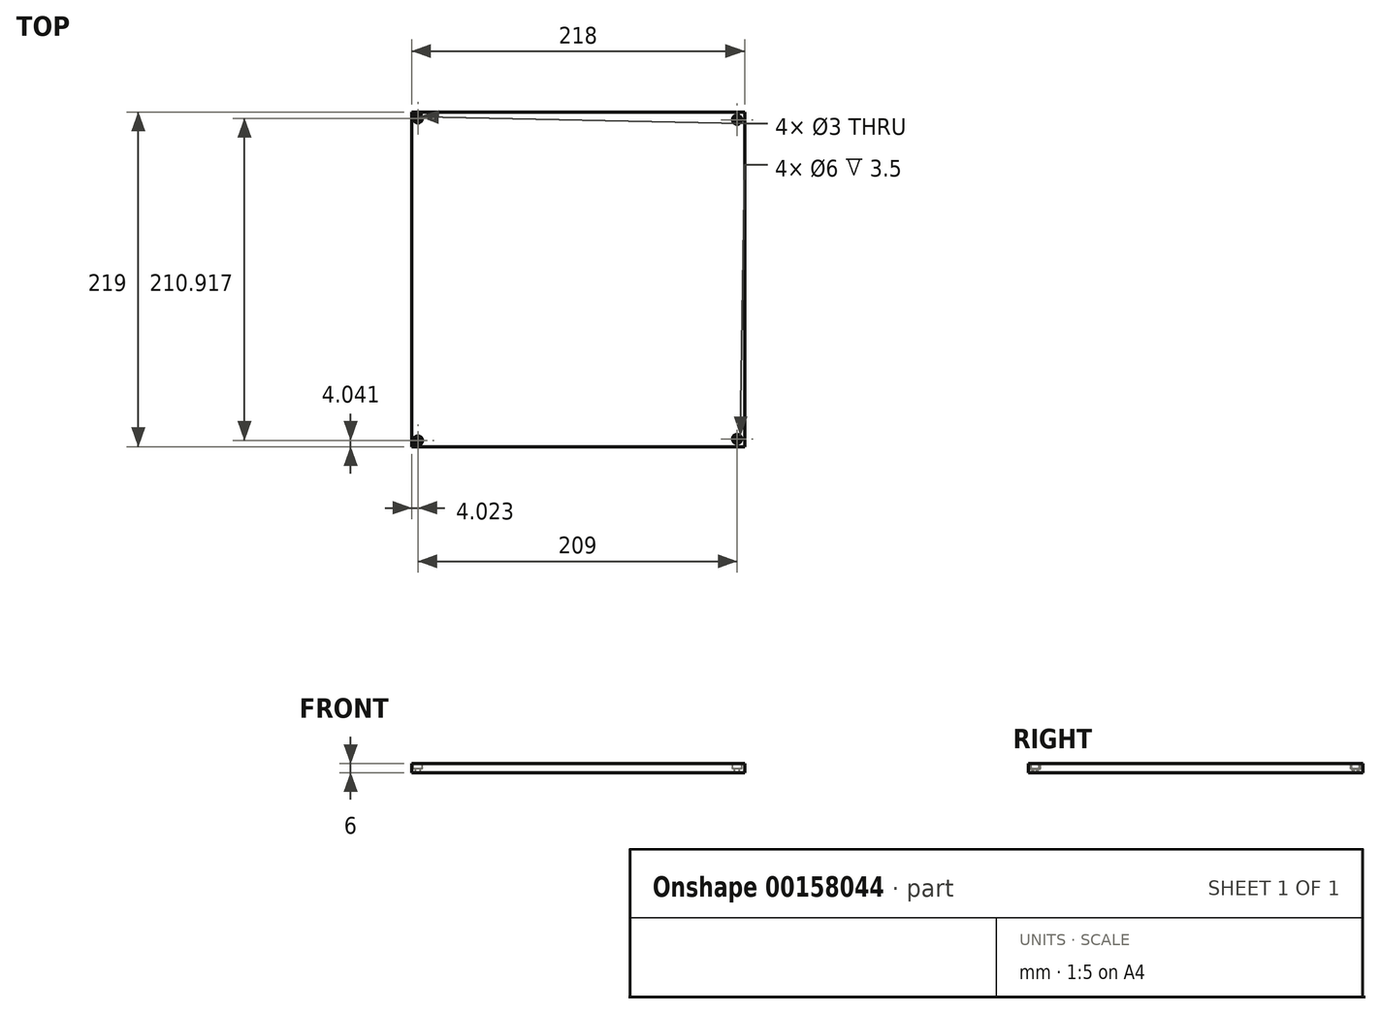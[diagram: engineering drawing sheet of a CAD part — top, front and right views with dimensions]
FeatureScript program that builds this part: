
annotation { "Feature Type Name" : "Feature", "Feature Type Description" : "" }
export const myFeature = defineFeature(function(context is Context, id is Id, definition is map)
    precondition{}
    {
        {
            var Q0;
            Q0=qCreatedBy(makeId("Top.planeOp"),FACE);
            var sketch = newSketch(context, id + "F0", { "sketchPlane" : qUnion([Q0])});
            skLineSegment(sketch, "E0.bottom", {"start": v(-109, 109.5) * mm, "end": v(109, 109.5) * mm});
            skLineSegment(sketch, "E0.top", {"start": v(-109, -109.5) * mm, "end": v(109, -109.5) * mm});
            skLineSegment(sketch, "E0.left", {"start": v(-109, 109.5) * mm, "end": v(-109, -109.5) * mm});
            skLineSegment(sketch, "E0.right", {"start": v(109, 109.5) * mm, "end": v(109, -109.5) * mm});
            skPoint(sketch, "E1", {"position": v(0, 109.5) * mm});
            skPoint(sketch, "E2", {"position": v(-109, 0) * mm});
            skSolve(sketch);
        }
        {
            var Q0;
            Q0 = qSketchRegion(id + "F0", true);
            extrude(context, id + "F1", {"entities" : qUnion([Q0]), "depth" : 6 * mm});
        }
        {
            var Q0;
            Q0=makeQuery(id+"F1.opExtrude","CAP_FACE",FACE,{"disambiguationData":[OSD([sQuery(id+"F0.wireOp",EDGE,"E0.bottom"),sQuery(id+"F0.wireOp",EDGE,"E0.top"),sQuery(id+"F0.wireOp",EDGE,"E0.left"),sQuery(id+"F0.wireOp",EDGE,"E0.right")])],"isStart":false});
            var sketch = newSketch(context, id + "F2", { "sketchPlane" : qUnion([Q0])});
            skLineSegment(sketch, "E3", {"start": v(-109, 109.5) * mm, "end": v(109, -109.5) * mm});
            skLineSegment(sketch, "E4", {"start": v(109, 109.5) * mm, "end": v(-109, -109.5) * mm});
            skPoint(sketch, "E5", {"position": v(-104.98, 105.46) * mm});
            skPoint(sketch, "E6", {"position": v(104.02, 104.5) * mm});
            skPoint(sketch, "E7", {"position": v(104.02, -104.5) * mm});
            skPoint(sketch, "E8", {"position": v(-104.98, -105.46) * mm});
            skCircle(sketch, "E9", {"center": v(-104.98, 105.46) * mm, "radius": 1.5 * mm});
            skCircle(sketch, "E10", {"center": v(104.02, 104.5) * mm, "radius": 1.5 * mm});
            skCircle(sketch, "E11", {"center": v(104.02, -104.5) * mm, "radius": 1.5 * mm});
            skCircle(sketch, "E12", {"center": v(-104.98, -105.46) * mm, "radius": 1.5 * mm});
            skSolve(sketch);
        }
        {
            var Q0;
            Q0 = qSketchRegion(id + "F2", true);
            var Q1;
            Q1=makeQuery(id+"F1.opExtrude","CAP_FACE",FACE,{"disambiguationData":[OSD([sQuery(id+"F0.wireOp",EDGE,"E0.bottom"),sQuery(id+"F0.wireOp",EDGE,"E0.top"),sQuery(id+"F0.wireOp",EDGE,"E0.left"),sQuery(id+"F0.wireOp",EDGE,"E0.right")])],"isStart":true});
            extrude(context, id + "F3", {"entities" : qUnion([Q0]), "operationType" : NewBodyOperationType.REMOVE, "endBound" : BoundingType.UP_TO_SURFACE, "oppositeDirection" : true, "endBoundEntityFace" : qUnion([Q1]), "depth" : 25 * mm});
        }
        {
            var Q0;
            Q0=makeQuery(id+"F1.opExtrude","CAP_FACE",FACE,{"disambiguationData":[OSD([sQuery(id+"F0.wireOp",EDGE,"E0.bottom"),sQuery(id+"F0.wireOp",EDGE,"E0.top"),sQuery(id+"F0.wireOp",EDGE,"E0.left"),sQuery(id+"F0.wireOp",EDGE,"E0.right")])],"isStart":false});
            var sketch = newSketch(context, id + "F4", { "sketchPlane" : qUnion([Q0])});
            skCircle(sketch, "E13", {"center": v(-104.98, 105.46) * mm, "radius": 3 * mm});
            skCircle(sketch, "E14", {"center": v(104.02, 104.5) * mm, "radius": 3 * mm});
            skCircle(sketch, "E15", {"center": v(104.02, -104.5) * mm, "radius": 3 * mm});
            skCircle(sketch, "E16", {"center": v(-104.98, -105.46) * mm, "radius": 3 * mm});
            skSolve(sketch);
        }
        {
            var Q0;
            Q0 = qSketchRegion(id + "F4", true);
            extrude(context, id + "F5", {"entities" : qUnion([Q0]), "operationType" : NewBodyOperationType.REMOVE, "oppositeDirection" : true, "depth" : 3.5 * mm});
        }
    });
